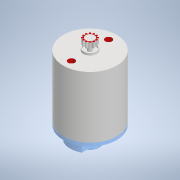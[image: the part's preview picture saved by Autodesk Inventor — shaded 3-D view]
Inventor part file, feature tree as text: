
AUTODESK INVENTOR PART (.ipt)
format: ipt  version: 2020 (Build 240168000, 168)  size: 235,008 bytes
history: native  units: mm
features: extrude x11, sketch x11, other x2, pattern_circular x1
ambient origin geometry x8: Origin, YZ Plane, XZ Plane, XY Plane, X Axis, Y Axis, Z Axis, Center Point
bodies: Body1 (feature_tree), Body2 (feature_tree)
feature tree (25):
  other  "Bryła1"
  extrude  "Wyciągnięcie proste1"  Depth=24.4mm
  extrude  "Wyciągnięcie proste2"  Depth=28.0mm TaperAngle=0.0deg
  extrude  "Wyciągnięcie proste3"  Depth=6.0mm
  extrude  "Wyciągnięcie proste4"  Depth=1.0mm TaperAngle=0.0deg
  extrude  "Wyciągnięcie proste5"  Depth=5.5mm
  extrude  "Wyciągnięcie proste6"  Depth=1.0mm TaperAngle=0.0deg
  extrude  "Wyciągnięcie proste7"  Depth=2.0mm
  pattern_circular  "Szyk kołowy1"  [2 undecoded]
  extrude  "Wyciągnięcie proste8"  Depth=5.75mm
  extrude  "Wyciągnięcie proste9"  Depth=2.5mm TaperAngle=0.0deg
  extrude  "Wyciągnięcie proste10"  Depth=4.0mm
  extrude  "Wyciągnięcie proste11"  TaperAngle=30.0deg  [1 undecoded]
  sketch  "Szkic1"
  sketch  "Szkic2"
  sketch  "Szkic3"
  sketch  "Szkic4"
  sketch  "Szkic5"
  sketch  "Szkic6"
  sketch  "Szkic7"
  sketch  "Szkic8"
  sketch  "Szkic9"
  other  "Bryła2"
  sketch  "Szkic10"
  sketch  "Szkic11"
note: 3 required parameter values undecoded (feature->parameter linkage not recoverable at this tier; creation-order binding heuristic only, values carry confidence <= 0.55)
